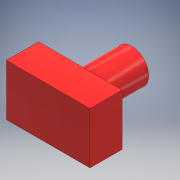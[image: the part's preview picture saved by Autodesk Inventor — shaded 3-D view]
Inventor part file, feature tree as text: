
AUTODESK INVENTOR PART (.ipt)
format: ipt  version: 2018 (Build 220112000, 112)  size: 107,008 bytes
history: native  units: mm
features: extrude x2, sketch x2, projected_geometry x1
ambient origin geometry x8: Origin, YZ Plane, XZ Plane, XY Plane, X Axis, Y Axis, Z Axis, Center Point
bodies: Solid1 (feature_tree)
feature tree (5):
  extrude  "Extrusion1"  Depth=5.0mm
  extrude  "Extrusion2"  Depth=8.0mm
  sketch  "Sketch1"  dims[d0=13.0mm d1=5.0mm]
  sketch  "Sketch2"  dims[d2=8.0mm d3=0.0mm d4=5.29mm d5=8.0mm d6=0.0mm]
  projected_geometry  "Projected Loop1"
